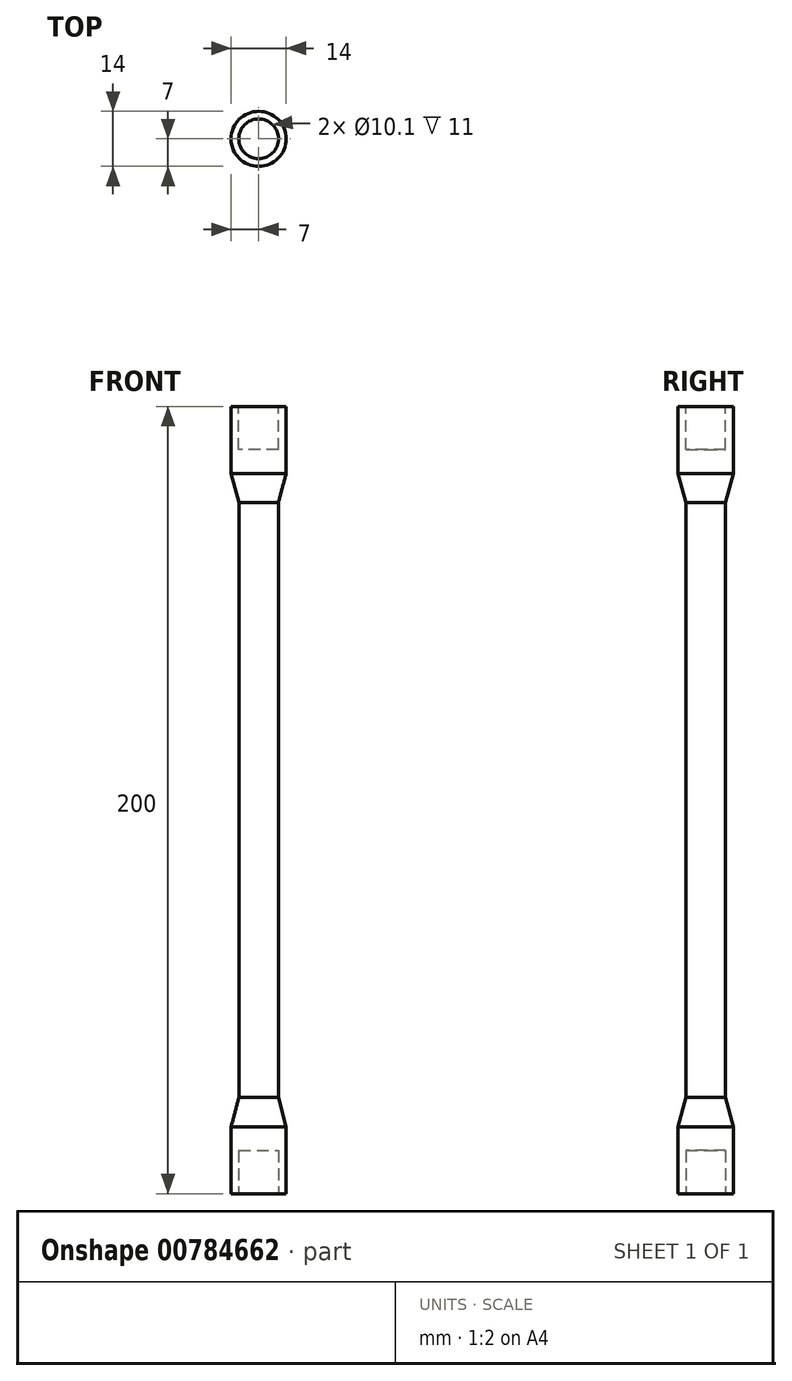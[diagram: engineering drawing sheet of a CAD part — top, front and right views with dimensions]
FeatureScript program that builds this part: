
annotation { "Feature Type Name" : "Feature", "Feature Type Description" : "" }
export const myFeature = defineFeature(function(context is Context, id is Id, definition is map)
    precondition{}
    {
        {
            var Q0;
            Q0=qCreatedBy(makeId("Top.planeOp"),FACE);
            var sketch = newSketch(context, id + "F0", { "sketchPlane" : qUnion([Q0])});
            skCircle(sketch, "E0", {"center": v(0, 0) * mm, "radius": 5 * mm});
            skSolve(sketch);
        }
        {
            var Q0;
            Q0=makeQuery(id+"F0.imprint","IMPRINT",FACE,{"disambiguationData":[TD([[makeQuery(id+"F0.imprint","IMPRINT",EDGE,{"derivedFrom":sQuery(id+"F0.wireOp",EDGE,"E0")}),1.0]])]});
            extrude(context, id + "F1", {"entities" : qUnion([Q0]), "offsetDistance" : 25 * mm, "depth" : 150 * mm, "hasSecondDirection" : true, "secondDirectionOppositeDirection" : true, "secondDirectionDepth" : 50 * mm, "symmetric" : true});
        }
        {
            var Q0;
            Q0=makeQuery(id+"F1.opExtrude","CAP_FACE",FACE,{"disambiguationData":[OSD([sQuery(id+"F0.wireOp",EDGE,"E0")])],"isStart":false});
            var sketch = newSketch(context, id + "F2", { "sketchPlane" : qUnion([Q0])});
            skCircle(sketch, "E1", {"center": v(0, 0) * mm, "radius": 7 * mm});
            skSolve(sketch);
        }
        {
            var Q0;
            Q0=makeQuery(id+"F1.opExtrude","CAP_FACE",FACE,{"disambiguationData":[OSD([sQuery(id+"F0.wireOp",EDGE,"E0")])],"isStart":true});
            var sketch = newSketch(context, id + "F3", { "sketchPlane" : qUnion([Q0])});
            skCircle(sketch, "E2", {"center": v(0, 0) * mm, "radius": 7 * mm});
            skSolve(sketch);
        }
        {
            var Q0;
            Q0=makeQuery(id+"F2.imprint","IMPRINT",FACE,{"disambiguationData":[TD([[makeQuery(id+"F2.imprint","IMPRINT",EDGE,{"derivedFrom":sQuery(id+"F2.wireOp",EDGE,"E1")}),1.0]])]});
            var Q1;
            Q1=makeQuery(id+"F2.imprint","IMPRINT",FACE,{"disambiguationData":[TD([[makeQuery(id+"F2.imprint","IMPRINT",EDGE,{"derivedFrom":makeQuery(id+"F1.opExtrude","CAP_EDGE",EDGE,{"disambiguationData":[OSD([sQuery(id+"F0.wireOp",EDGE,"E0")])],"isStart":false})}),1.0]])]});
            extrude(context, id + "F4", {"entities" : qUnion([Q0, Q1]), "operationType" : NewBodyOperationType.ADD, "depth" : 25 * mm});
        }
        {
            var Q0;
            Q0=makeQuery(id+"F3.imprint","IMPRINT",FACE,{"disambiguationData":[TD([[makeQuery(id+"F3.imprint","IMPRINT",EDGE,{"derivedFrom":makeQuery(id+"F1.opExtrude","CAP_EDGE",EDGE,{"disambiguationData":[OSD([sQuery(id+"F0.wireOp",EDGE,"E0")])],"isStart":true})}),-1.0]])]});
            var Q1;
            Q1=makeQuery(id+"F3.imprint","IMPRINT",FACE,{"disambiguationData":[TD([[makeQuery(id+"F3.imprint","IMPRINT",EDGE,{"derivedFrom":sQuery(id+"F3.wireOp",EDGE,"E2")}),1.0]])]});
            extrude(context, id + "F5", {"entities" : qUnion([Q0, Q1]), "operationType" : NewBodyOperationType.ADD, "depth" : 25 * mm});
        }
        {
            var Q0;
            Q0=makeQuery(id+"F5.opExtrude","CAP_EDGE",EDGE,{"disambiguationData":[OSD([sQuery(id+"F3.wireOp",EDGE,"E2")])],"isStart":true});
            var Q1;
            Q1=makeQuery(id+"F4.opExtrude","CAP_EDGE",EDGE,{"disambiguationData":[OSD([sQuery(id+"F2.wireOp",EDGE,"E1")])],"isStart":true});
            chamfer(context, id + "F6", {"entities" : qUnion([Q0, Q1]), "chamferType" : ChamferType.OFFSET_ANGLE, "width" : 8 * mm, "oppositeDirection" : false, "angle" : 15 * degree, "tangentPropagation" : true});
        }
        {
            var Q0;
            Q0=makeQuery(id+"F5.opExtrude","CAP_FACE",FACE,{"disambiguationData":[OSD([sQuery(id+"F3.wireOp",EDGE,"E2")])],"isStart":false});
            var sketch = newSketch(context, id + "F7", { "sketchPlane" : qUnion([Q0])});
            skCircle(sketch, "E3", {"center": v(0, 0) * mm, "radius": 5.05 * mm});
            skSolve(sketch);
        }
        {
            var Q0;
            Q0=makeQuery(id+"F7.imprint","IMPRINT",FACE,{"disambiguationData":[TD([[makeQuery(id+"F7.imprint","IMPRINT",EDGE,{"derivedFrom":sQuery(id+"F7.wireOp",EDGE,"E3")}),1.0]])]});
            extrude(context, id + "F8", {"entities" : qUnion([Q0]), "operationType" : NewBodyOperationType.REMOVE, "oppositeDirection" : true, "depth" : 11 * mm, "offsetDistance" : 25 * mm});
        }
        {
            var Q0;
            Q0=makeQuery(id+"F4.opExtrude","CAP_FACE",FACE,{"disambiguationData":[OSD([sQuery(id+"F2.wireOp",EDGE,"E1")])],"isStart":false});
            var sketch = newSketch(context, id + "F9", { "sketchPlane" : qUnion([Q0])});
            skCircle(sketch, "E4", {"center": v(0, 0) * mm, "radius": 5.05 * mm});
            skSolve(sketch);
        }
        {
            var Q0;
            Q0=makeQuery(id+"F9.imprint","IMPRINT",FACE,{"disambiguationData":[TD([[makeQuery(id+"F9.imprint","IMPRINT",EDGE,{"derivedFrom":sQuery(id+"F9.wireOp",EDGE,"E4")}),1.0]])]});
            extrude(context, id + "F10", {"entities" : qUnion([Q0]), "operationType" : NewBodyOperationType.REMOVE, "oppositeDirection" : true, "depth" : 11 * mm, "offsetDistance" : 25 * mm});
        }
    });
